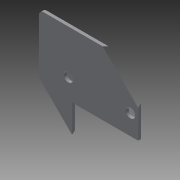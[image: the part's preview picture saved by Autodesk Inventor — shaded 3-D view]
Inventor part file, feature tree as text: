
AUTODESK INVENTOR PART (.ipt)
format: ipt  version: 2015 SP1 (Build 190203100, 203)  size: 100,864 bytes
history: native  units: in
note: dims shown in document units (in); Inventor stores cm internally (conversion verified against a paired STEP export)
features: reference x4, sketch x2, extrude x1, hole x1
ambient origin geometry x8: Origin, YZ Plane, XZ Plane, XY Plane, X Axis, Y Axis, Z Axis, Center Point
bodies: Solid1 (feature_tree)
feature tree (8):
  extrude  "Extrusion1"  Depth=0.0787in
  hole  "Hole1"  [1 undecoded]
  sketch  "Sketch1"  dims[d0=0.0787in d1=1.7717in]
  sketch  "Sketch2"  dims[d3=1.565in d5=0.1772in d6=1.8406in d7=0.1772in d8=0.0472in d9=0.0in d10=0.1495in d11=0.2362in d12=0.279in d13=0.0787in d14=0.5635in d15=0.315in d16=0.8108in d19=0.315in]
  reference  "Reference1"
  reference  "Reference2"
  reference  "Reference3"
  reference  "Reference4"
note: 1 required parameter value undecoded (feature->parameter linkage not recoverable at this tier; creation-order binding heuristic only, values carry confidence <= 0.55)
